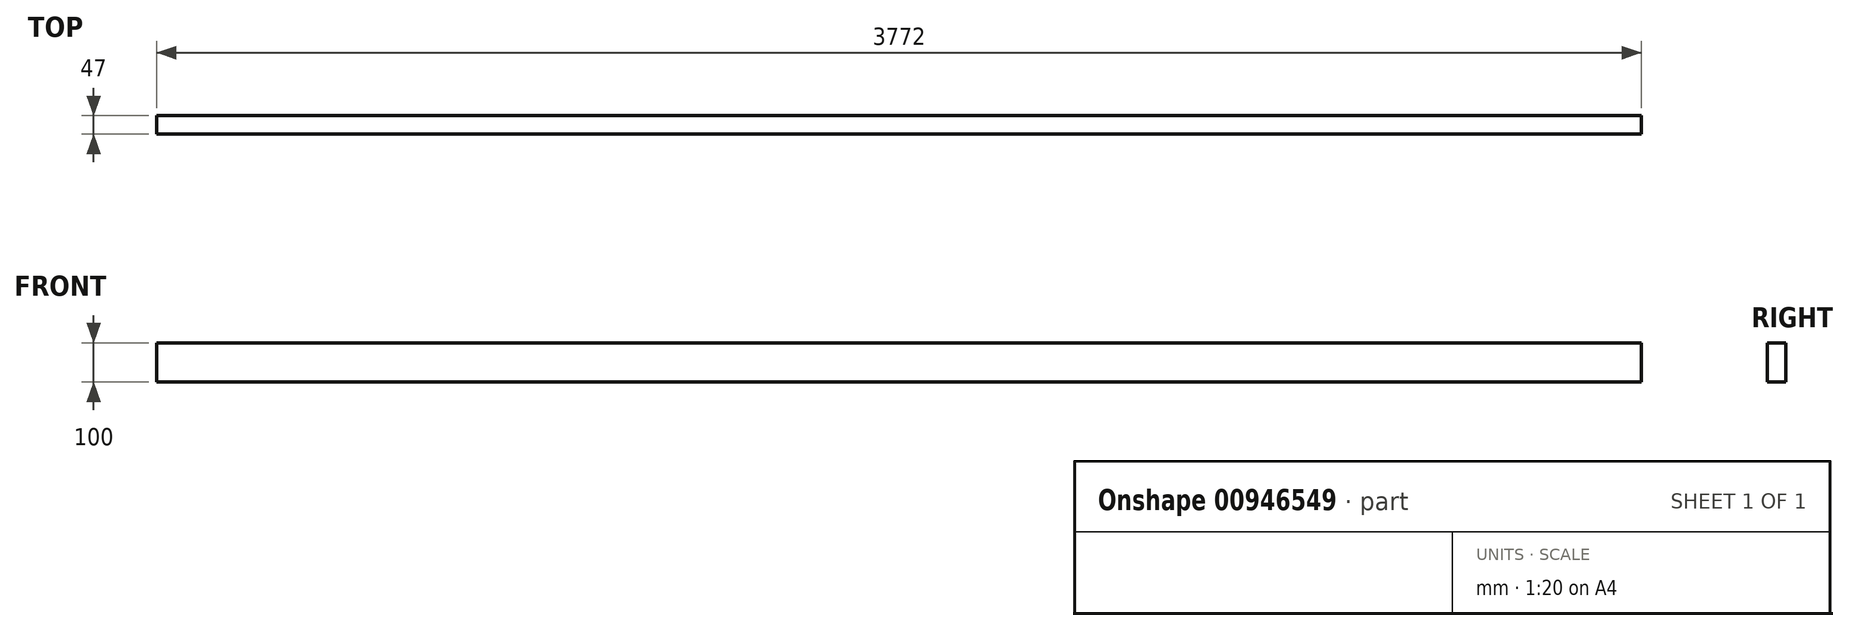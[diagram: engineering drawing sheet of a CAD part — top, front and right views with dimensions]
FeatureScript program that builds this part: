
annotation { "Feature Type Name" : "Feature", "Feature Type Description" : "" }
export const myFeature = defineFeature(function(context is Context, id is Id, definition is map)
    precondition{}
    {
        {
            var Q0;
            Q0=qCreatedBy(makeId("Right.planeOp"),FACE);
            var sketch = newSketch(context, id + "F0", { "sketchPlane" : qUnion([Q0])});
            skLineSegment(sketch, "E0.bottom", {"start": v(0, 0) * mm, "end": v(-47, 0) * mm});
            skLineSegment(sketch, "E0.top", {"start": v(0, 100) * mm, "end": v(-47, 100) * mm});
            skLineSegment(sketch, "E0.left", {"start": v(0, 0) * mm, "end": v(0, 100) * mm});
            skLineSegment(sketch, "E0.right", {"start": v(-47, 0) * mm, "end": v(-47, 100) * mm});
            skSolve(sketch);
        }
        {
            var Q0;
            Q0=qSketchRegion(id+"F0",true);
            extrude(context, id + "F1", {"entities" : qUnion([Q0]), "depth" : 3772 * mm, "offsetDistance" : 25 * mm});
        }
    });
